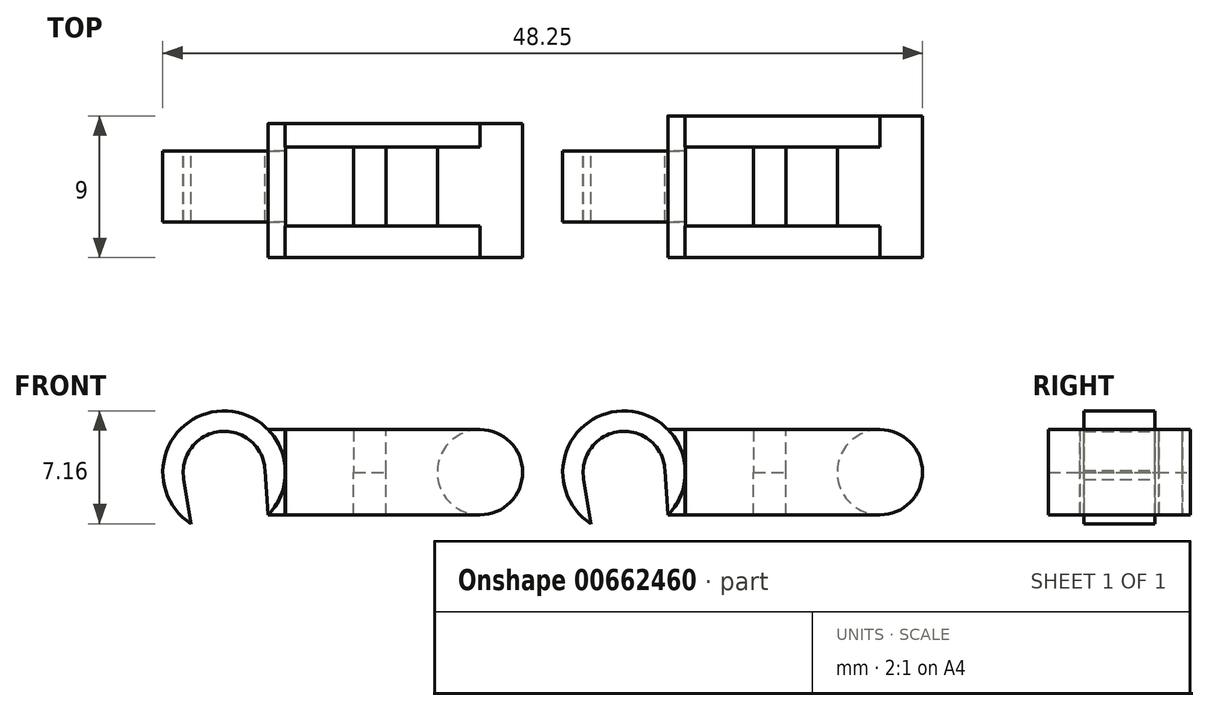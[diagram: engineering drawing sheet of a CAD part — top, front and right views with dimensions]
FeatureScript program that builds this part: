
annotation { "Feature Type Name" : "Feature", "Feature Type Description" : "" }
export const myFeature = defineFeature(function(context is Context, id is Id, definition is map)
    precondition{}
    {
        {
            var Q0;
            Q0=qCreatedBy(makeId("Front.planeOp"),FACE);
            var sketch = newSketch(context, id + "F0", { "sketchPlane" : qUnion([Q0])});
            skLineSegment(sketch, "E0.bottom", {"start": v(2.17, 2.7) * mm, "end": v(0.1, 2.7) * mm});
            skLineSegment(sketch, "E0.left", {"start": v(8.12, 2.7) * mm, "end": v(8.12, -2.7) * mm});
            skPoint(sketch, "E0.middle", {"position": v(0, 0) * mm});
            skCircle(sketch, "E1", {"center": v(8.12, 0) * mm, "radius": 2.7 * mm});
            skLineSegment(sketch, "E2", {"start": v(8.12, 0) * mm, "end": v(5.42, 0) * mm});
            skLineSegment(sketch, "E3", {"start": v(2.17, 0) * mm, "end": v(2.17, 2.7) * mm});
            skLineSegment(sketch, "E4", {"start": v(2.17, 0) * mm, "end": v(2.17, -2.7) * mm});
            skLineSegment(sketch, "E5.left", {"start": v(2.17, 2.7) * mm, "end": v(2.17, -2.7) * mm});
            skLineSegment(sketch, "E6", {"start": v(0.1, 2.7) * mm, "end": v(0.1, -2.7) * mm});
            skLineSegment(sketch, "E7", {"start": v(-4.23, 2.7) * mm, "end": v(-4.23, -2.73) * mm});
            skLineSegment(sketch, "E8.trimOffspring", {"start": v(-4.23, -2.73) * mm, "end": v(-5.34, -2.72) * mm});
            skLineSegment(sketch, "E9.trimOffspring", {"start": v(-4.23, 2.7) * mm, "end": v(-5.33, 2.7) * mm});
            skLineSegment(sketch, "E10", {"start": v(2.17, -2.7) * mm, "end": v(0.1, -2.7) * mm});
            skArc(sketch, "E11", {"start": v(-5.33, 2.7) * mm, "mid": v(-11.13, 2.47) * mm, "end": v(-10.24, -3.27) * mm});
            skArc(sketch, "E12", {"start": v(-5.53, 0.12) * mm, "mid": v(-8.4, 2.58) * mm, "end": v(-10.69, -0.45) * mm});
            skPoint(sketch, "E13.orphan", {"position": v(-8.12, -2.7) * mm});
            skPoint(sketch, "E0.right.start.orphan", {"position": v(-8.12, 2.7) * mm});
            skLineSegment(sketch, "E14", {"start": v(-5.34, -2.72) * mm, "end": v(-5.53, 0.22) * mm});
            skLineSegment(sketch, "E15", {"start": v(-10.33, -2.7) * mm, "end": v(-10.69, -0.45) * mm});
            skLineSegment(sketch, "E16", {"start": v(-10.69, -0.45) * mm, "end": v(-10.33, -2.7) * mm});
            skLineSegment(sketch, "E17", {"start": v(-10.69, -0.45) * mm, "end": v(-10.24, -3.27) * mm});
            skPoint(sketch, "E18.end.orphan", {"position": v(-10.33, -3.21) * mm});
            skArc(sketch, "E19", {"start": v(-5.34, -2.72) * mm, "mid": v(-8.56, 3.87) * mm, "end": v(-10.24, -3.27) * mm});
            skLineSegment(sketch, "E20", {"start": v(0, 0) * mm, "end": v(-4.23, 0) * mm});
            skLineSegment(sketch, "E21", {"start": v(-4.23, 0) * mm, "end": v(-4.23, 2.7) * mm});
            skLineSegment(sketch, "E22", {"start": v(0, 0) * mm, "end": v(8.12, 0) * mm});
            skSolve(sketch);
        }
        {
            var Q0;
            {var subQ0=sQuery(id+"F0.wireOp",EDGE,"E9.trimOffspring");Q0=makeQuery(id+"F0.imprint","IMPRINT",FACE,{"disambiguationData":[TD([[makeQuery(id+"F0.imprint","IMPRINT",EDGE,{"derivedFrom":subQ0}),1.0]])]});}
            var Q1;
            {var subQ0=sQuery(id+"F0.wireOp",EDGE,"E8.trimOffspring");Q1=makeQuery(id+"F0.imprint","IMPRINT",FACE,{"disambiguationData":[TD([[makeQuery(id+"F0.imprint","IMPRINT",EDGE,{"derivedFrom":subQ0}),-1.0]])]});}
            var Q2;
            {var subQ3=sQuery(id+"F0.wireOp",EDGE,"E2");Q2=makeQuery(id+"F0.imprint","IMPRINT",FACE,{"disambiguationData":[TD([[makeQuery(id+"F0.imprint","IMPRINT",EDGE,{"derivedFrom":subQ3}),-1.0]])]});}
            var Q3;
            {var subQ3=sQuery(id+"F0.wireOp",EDGE,"E2");Q3=makeQuery(id+"F0.imprint","IMPRINT",FACE,{"disambiguationData":[TD([[makeQuery(id+"F0.imprint","IMPRINT",EDGE,{"derivedFrom":subQ3}),1.0]])]});}
            var Q4;
            {var subQ0=sQuery(id+"F0.wireOp",EDGE,"E1");var subQ1=sQuery(id+"F0.wireOp",EDGE,"E0.left");var subQ2=makeQuery(id+"F0.imprint","INTERSECT",VERTEX,{"disambiguationData":[OD(0.0)],"derivedFrom":[subQ1,subQ0]});Q4=makeQuery(id+"F0.imprint","IMPRINT",FACE,{"disambiguationData":[TD([[makeQuery(id+"F0.imprint","IMPRINT",EDGE,{"disambiguationData":[TD([[subQ2,-1.0]])],"derivedFrom":subQ1}),1.0]])]});}
            extrude(context, id + "F1", {"entities" : qUnion([Q0, Q1, Q2, Q3, Q4]), "depth" : 4.5 * mm, "offsetDistance" : 25.4 * mm, "hasSecondDirection" : true, "secondDirectionOppositeDirection" : true, "secondDirectionDepth" : 4.5 * mm});
        }
        {
            var Q0;
            {var subQ5=sQuery(id+"F0.wireOp",EDGE,"E12");Q0=makeQuery(id+"F0.imprint","IMPRINT",FACE,{"disambiguationData":[TD([[makeQuery(id+"F0.imprint","IMPRINT",EDGE,{"derivedFrom":subQ5}),-1.0]])]});}
            var Q1;
            Q1=makeQuery(id+"F0.imprint","IMPRINT",FACE,{"disambiguationData":[TD([[makeQuery(id+"F0.imprint","IMPRINT",EDGE,{"derivedFrom":sQuery(id+"F0.wireOp",EDGE,"E0.bottom")}),1.0]])]});
            extrude(context, id + "F2", {"entities" : qUnion([Q0, Q1]), "depth" : 2.5 * mm, "offsetDistance" : 25.4 * mm, "hasSecondDirection" : true, "secondDirectionOppositeDirection" : true, "secondDirectionDepth" : 2.5 * mm});
        }
        {
            var Q0;
            Q0=qCreatedBy(makeId("Front.planeOp"),FACE);
            cPlane(context, id + "F3", {"entities" : qUnion([Q0]), "cplaneType" : CPlaneType.OFFSET, "offset" : 4.5 * mm, "width" : 152.4 * mm, "height" : 152.4 * mm});
        }
        {
            var Q0;
            Q0=qCreatedBy(id+"F3.planeOp",FACE);
            var sketch = newSketch(context, id + "F4", { "sketchPlane" : qUnion([Q0])});
            skLineSegment(sketch, "E23.bottom", {"start": v(0, 0) * mm, "end": v(8.13, 0) * mm});
            skLineSegment(sketch, "E23.top", {"start": v(0, 2.72) * mm, "end": v(8.13, 2.72) * mm});
            skLineSegment(sketch, "E23.left", {"start": v(0, 0) * mm, "end": v(0, 2.72) * mm});
            skLineSegment(sketch, "E23.right", {"start": v(8.13, 0) * mm, "end": v(8.13, 2.72) * mm});
            skLineSegment(sketch, "E24.bottom", {"start": v(0, 2.72) * mm, "end": v(-4.24, 2.72) * mm});
            skLineSegment(sketch, "E24.top", {"start": v(0, 0) * mm, "end": v(-4.24, 0) * mm});
            skLineSegment(sketch, "E24.left", {"start": v(0, 2.72) * mm, "end": v(0, 0) * mm});
            skLineSegment(sketch, "E24.right", {"start": v(-4.24, 2.72) * mm, "end": v(-4.24, 0) * mm});
            skLineSegment(sketch, "E25.MirrorCS", {"start": v(-4.24, -2.72) * mm, "end": v(-4.24, 0) * mm});
            skLineSegment(sketch, "E26.MirrorCS", {"start": v(0, -2.72) * mm, "end": v(-4.24, -2.72) * mm});
            skLineSegment(sketch, "E27.MirrorCS", {"start": v(0, -2.72) * mm, "end": v(8.13, -2.72) * mm});
            skLineSegment(sketch, "E28.MirrorCS", {"start": v(8.13, 0) * mm, "end": v(8.13, -2.72) * mm});
            skLineSegment(sketch, "E29.MirrorCS", {"start": v(0, -2.72) * mm, "end": v(0, 0) * mm});
            skSolve(sketch);
        }
        {
            var Q0;
            Q0 = qSketchRegion(id + "F4", true);
            extrude(context, id + "F5", {"entities" : qUnion([Q0]), "oppositeDirection" : true, "depth" : 2 * mm, "offsetDistance" : 25.4 * mm});
        }
        {
            var Q0;
            Q0=makeQuery(id+"F5.opExtrude","SWEPT_BODY",BODY,{"disambiguationData":[OSD([sQuery(id+"F4.wireOp",EDGE,"E23.top"),sQuery(id+"F4.wireOp",EDGE,"E23.right"),sQuery(id+"F4.wireOp",EDGE,"E24.bottom"),sQuery(id+"F4.wireOp",EDGE,"E24.right"),sQuery(id+"F4.wireOp",EDGE,"E26.MirrorCS"),sQuery(id+"F4.wireOp",EDGE,"E27.MirrorCS"),sQuery(id+"F4.wireOp",EDGE,"E28.MirrorCS"),sQuery(id+"F4.wireOp",EDGE,"E25.MirrorCS")])]});
            var Q1;
            Q1=qCreatedBy(makeId("Front.planeOp"),FACE);
            mirror(context, id + "F6", {"entities" : qUnion([Q0]), "mirrorPlane" : qUnion([Q1])});
        }
        {
            var Q0;
            {var subQ0=sQuery(id+"F0.wireOp",EDGE,"E1");var subQ1=sQuery(id+"F0.wireOp",EDGE,"E0.left");var subQ2=makeQuery(id+"F0.imprint","INTERSECT",VERTEX,{"disambiguationData":[OD(1.0)],"derivedFrom":[subQ1,subQ0]});Q0=makeQuery(id+"F0.imprint","IMPRINT",FACE,{"disambiguationData":[TD([[makeQuery(id+"F0.imprint","IMPRINT",EDGE,{"disambiguationData":[TD([[subQ2,1.0]])],"derivedFrom":subQ1}),-1.0]])]});}
            var Q1;
            {var subQ0=sQuery(id+"F0.wireOp",EDGE,"E1");var subQ1=sQuery(id+"F0.wireOp",EDGE,"E0.left");var subQ2=makeQuery(id+"F0.imprint","INTERSECT",VERTEX,{"disambiguationData":[OD(0.0)],"derivedFrom":[subQ1,subQ0]});Q1=makeQuery(id+"F0.imprint","IMPRINT",FACE,{"disambiguationData":[TD([[makeQuery(id+"F0.imprint","IMPRINT",EDGE,{"disambiguationData":[TD([[subQ2,-1.0]])],"derivedFrom":subQ1}),-1.0]])]});}
            extrude(context, id + "F7", {"entities" : qUnion([Q0, Q1]), "operationType" : NewBodyOperationType.ADD, "depth" : 3 * mm, "offsetDistance" : 25.4 * mm, "hasSecondDirection" : true, "secondDirectionOppositeDirection" : true, "secondDirectionDepth" : 3 * mm});
        }
        {
            var Q0;
            Q0=makeQuery(id+"F2.opExtrude","SWEPT_FACE",FACE,{"disambiguationData":[OSD([sQuery(id+"F0.wireOp",EDGE,"E22")])]});
            var Q1;
            Q1=makeQuery(id+"F6.opPattern","COPY",FACE,{"derivedFrom":makeQuery(id+"F5.opExtrude","SWEPT_FACE",FACE,{"disambiguationData":[OSD([sQuery(id+"F4.wireOp",EDGE,"E26.MirrorCS"),sQuery(id+"F4.wireOp",EDGE,"E27.MirrorCS")])]}),"instanceName":"1"});
            extrude(context, id + "F8", {"entities" : qUnion([Q0]), "endBound" : BoundingType.UP_TO_SURFACE, "depth" : 2.5 * mm, "endBoundEntityFace" : qUnion([Q1]), "offsetDistance" : 25.4 * mm});
        }
        {
            var Q0;
            Q0=makeQuery(id+"F2.opExtrude","CAP_FACE",FACE,{"disambiguationData":[OSD([sQuery(id+"F0.wireOp",EDGE,"E12"),sQuery(id+"F0.wireOp",EDGE,"E14"),sQuery(id+"F0.wireOp",EDGE,"E17"),sQuery(id+"F0.wireOp",EDGE,"E19"),sQuery(id+"F0.wireOp",EDGE,"E21")])],"isStart":false});
            extrude(context, id + "F9", {"entities" : qUnion([Q0]), "operationType" : NewBodyOperationType.REMOVE, "oppositeDirection" : true, "depth" : .25 * mm, "offsetDistance" : 25.4 * mm});
        }
        {
            var Q0;
            Q0=makeQuery(id+"F2.opExtrude","CAP_FACE",FACE,{"disambiguationData":[OSD([sQuery(id+"F0.wireOp",EDGE,"E12"),sQuery(id+"F0.wireOp",EDGE,"E14"),sQuery(id+"F0.wireOp",EDGE,"E17"),sQuery(id+"F0.wireOp",EDGE,"E19"),sQuery(id+"F0.wireOp",EDGE,"E21")])],"isStart":true});
            extrude(context, id + "F10", {"entities" : qUnion([Q0]), "operationType" : NewBodyOperationType.REMOVE, "oppositeDirection" : true, "depth" : .25 * mm, "offsetDistance" : 25.4 * mm});
        }
        {
            var Q0;
            Q0=makeQuery(id+"F1.opExtrude","SWEPT_BODY",BODY,{"disambiguationData":[OSD([sQuery(id+"F0.wireOp",EDGE,"E0.left"),sQuery(id+"F0.wireOp",EDGE,"E1")])]});
            var Q1;
            Q1=makeQuery(id+"F2.opExtrude","SWEPT_BODY",BODY,{"disambiguationData":[OSD([sQuery(id+"F0.wireOp",EDGE,"E0.bottom"),sQuery(id+"F0.wireOp",EDGE,"E5.left"),sQuery(id+"F0.wireOp",EDGE,"E6"),sQuery(id+"F0.wireOp",EDGE,"E22")])]});
            var Q2;
            Q2=makeQuery(id+"F8.opExtrude","SWEPT_BODY",BODY,{"disambiguationData":[OSD([sQuery(id+"F0.wireOp",EDGE,"E22")])]});
            var Q3;
            Q3=makeQuery(id+"F2.opExtrude","SWEPT_BODY",BODY,{"disambiguationData":[OSD([sQuery(id+"F0.wireOp",EDGE,"E12"),sQuery(id+"F0.wireOp",EDGE,"E14"),sQuery(id+"F0.wireOp",EDGE,"E17"),sQuery(id+"F0.wireOp",EDGE,"E19"),sQuery(id+"F0.wireOp",EDGE,"E21")])]});
            var Q4;
            Q4=makeQuery(id+"F1.opExtrude","SWEPT_BODY",BODY,{"disambiguationData":[OSD([sQuery(id+"F0.wireOp",EDGE,"E7"),sQuery(id+"F0.wireOp",EDGE,"E8.trimOffspring"),sQuery(id+"F0.wireOp",EDGE,"E19")])]});
            var Q5;
            Q5=makeQuery(id+"F1.opExtrude","SWEPT_BODY",BODY,{"disambiguationData":[OSD([sQuery(id+"F0.wireOp",EDGE,"E9.trimOffspring"),sQuery(id+"F0.wireOp",EDGE,"E19"),sQuery(id+"F0.wireOp",EDGE,"E21")])]});
            transform(context, id + "F11", {"entities" : qUnion([Q0, Q1, Q2, Q3, Q4, Q5]), "transformType" : TransformType.TRANSLATION_3D, "dx" : 25.4 * mm, "dy" : 0 * mm, "dz" : 0 * mm, "makeCopy" : true});
        }
        {
            var Q0;
            Q0=makeQuery(id+"F7.boolean.opBoolean","MERGE",FACE,{"derivedFrom":[makeQuery(id+"F1.opExtrude","CAP_FACE",FACE,{"disambiguationData":[OSD([sQuery(id+"F0.wireOp",EDGE,"E0.left"),sQuery(id+"F0.wireOp",EDGE,"E1")])],"isStart":true}),makeQuery(id+"F6.opPattern","COPY",FACE,{"derivedFrom":makeQuery(id+"F5.opExtrude","CAP_FACE",FACE,{"disambiguationData":[OSD([sQuery(id+"F4.wireOp",EDGE,"E23.top"),sQuery(id+"F4.wireOp",EDGE,"E23.right"),sQuery(id+"F4.wireOp",EDGE,"E24.bottom"),sQuery(id+"F4.wireOp",EDGE,"E24.right"),sQuery(id+"F4.wireOp",EDGE,"E26.MirrorCS"),sQuery(id+"F4.wireOp",EDGE,"E27.MirrorCS"),sQuery(id+"F4.wireOp",EDGE,"E28.MirrorCS"),sQuery(id+"F4.wireOp",EDGE,"E25.MirrorCS")])],"isStart":true}),"instanceName":"1"})]});
            var Q1;
            Q1=makeQuery(id+"F1.opExtrude","CAP_FACE",FACE,{"disambiguationData":[OSD([sQuery(id+"F0.wireOp",EDGE,"E7"),sQuery(id+"F0.wireOp",EDGE,"E8.trimOffspring"),sQuery(id+"F0.wireOp",EDGE,"E19")])],"isStart":true});
            var Q2;
            Q2=makeQuery(id+"F1.opExtrude","CAP_FACE",FACE,{"disambiguationData":[OSD([sQuery(id+"F0.wireOp",EDGE,"E9.trimOffspring"),sQuery(id+"F0.wireOp",EDGE,"E19"),sQuery(id+"F0.wireOp",EDGE,"E21")])],"isStart":true});
            extrude(context, id + "F12", {"entities" : qUnion([Q0, Q1, Q2]), "operationType" : NewBodyOperationType.REMOVE, "oppositeDirection" : true, "depth" : .5 * mm, "offsetDistance" : 25.4 * mm});
        }
    });
